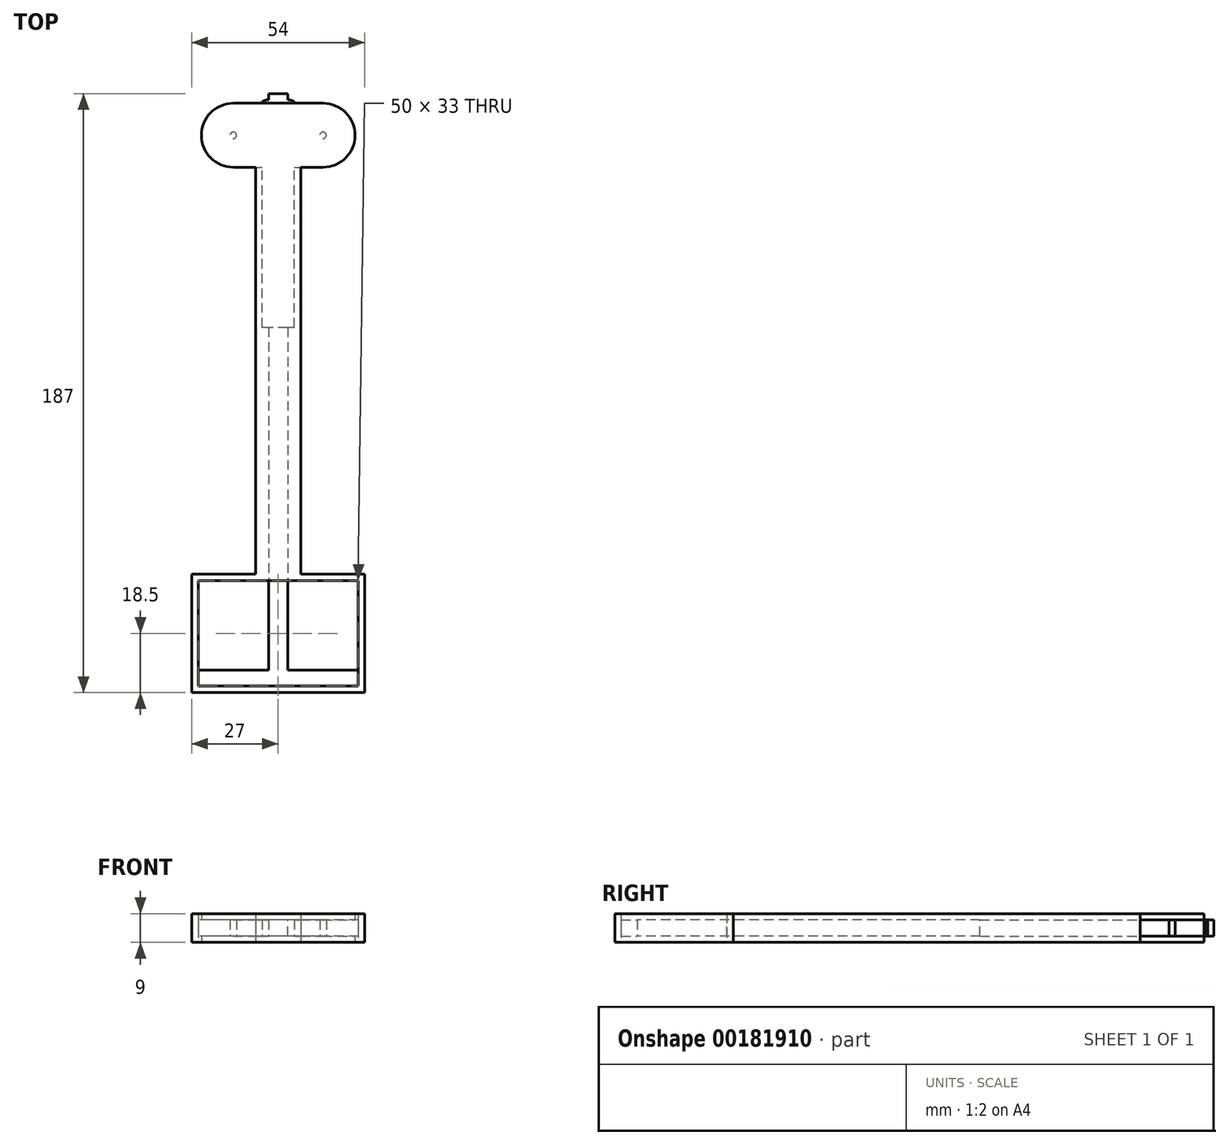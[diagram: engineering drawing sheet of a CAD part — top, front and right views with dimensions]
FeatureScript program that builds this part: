
annotation { "Feature Type Name" : "Feature", "Feature Type Description" : "" }
export const myFeature = defineFeature(function(context is Context, id is Id, definition is map)
    precondition{}
    {
        {
            var Q0;
            Q0=qCreatedBy(makeId("Top.planeOp"),FACE);
            var sketch = newSketch(context, id + "F0", { "sketchPlane" : qUnion([Q0])});
            skLineSegment(sketch, "E0.bottom", {"start": v(3, 13) * mm, "end": v(0, 13) * mm});
            skLineSegment(sketch, "E0.top", {"start": v(3, -167) * mm, "end": v(0, -167) * mm});
            skLineSegment(sketch, "E0.left", {"start": v(3, 13) * mm, "end": v(3, -167) * mm});
            skLineSegment(sketch, "E0.right", {"start": v(0, 13) * mm, "end": v(0, -167) * mm});
            skLineSegment(sketch, "E1", {"start": v(0, 10) * mm, "end": v(3, 10) * mm, "construction": true});
            skArc(sketch, "E2", {"start": v(3, 11.09) * mm, "mid": v(4.04, 10.94) * mm, "end": v(5, 10.5) * mm});
            skLineSegment(sketch, "E3", {"start": v(5, 10.5) * mm, "end": v(5, 10) * mm});
            skArc(sketch, "E4.MirrorCS", {"start": v(3, 8.91) * mm, "mid": v(4.04, 9.06) * mm, "end": v(5, 9.5) * mm});
            skLineSegment(sketch, "E5.MirrorCS", {"start": v(5, 9.5) * mm, "end": v(5, 10) * mm});
            skArc(sketch, "E6.1.0.0", {"start": v(3, 7.89) * mm, "mid": v(4.04, 7.74) * mm, "end": v(5, 7.3) * mm});
            skLineSegment(sketch, "E6.1.0.1", {"start": v(5, 7.3) * mm, "end": v(5, 6.8) * mm});
            skLineSegment(sketch, "E6.1.0.2", {"start": v(5, 6.3) * mm, "end": v(5, 6.8) * mm});
            skArc(sketch, "E6.1.0.3", {"start": v(3, 5.71) * mm, "mid": v(4.04, 5.86) * mm, "end": v(5, 6.3) * mm});
            skArc(sketch, "E6.2.0.0", {"start": v(3, 4.69) * mm, "mid": v(4.04, 4.54) * mm, "end": v(5, 4.1) * mm});
            skLineSegment(sketch, "E6.2.0.1", {"start": v(5, 4.1) * mm, "end": v(5, 3.6) * mm});
            skLineSegment(sketch, "E6.2.0.2", {"start": v(5, 3.1) * mm, "end": v(5, 3.6) * mm});
            skArc(sketch, "E6.2.0.3", {"start": v(3, 2.51) * mm, "mid": v(4.04, 2.66) * mm, "end": v(5, 3.1) * mm});
            skLineSegment(sketch, "E6.direction1", {"start": v(3, 7.39) * mm, "end": v(3, 4.19) * mm, "construction": true});
            skArc(sketch, "E7.0.3.0", {"start": v(3, 1.49) * mm, "mid": v(4.04, 1.34) * mm, "end": v(5, 0.9) * mm});
            skLineSegment(sketch, "E7.4.3.0", {"start": v(5, 0.9) * mm, "end": v(5, 0.4) * mm});
            skLineSegment(sketch, "E7.7.3.0", {"start": v(5, -0.1) * mm, "end": v(5, 0.4) * mm});
            skArc(sketch, "E7.10.3.0", {"start": v(3, -0.69) * mm, "mid": v(4.04, -0.54) * mm, "end": v(5, -0.1) * mm});
            skArc(sketch, "E7.0.4.0", {"start": v(3, -1.71) * mm, "mid": v(4.04, -1.86) * mm, "end": v(5, -2.3) * mm});
            skLineSegment(sketch, "E7.4.4.0", {"start": v(5, -2.3) * mm, "end": v(5, -2.8) * mm});
            skLineSegment(sketch, "E7.7.4.0", {"start": v(5, -3.3) * mm, "end": v(5, -2.8) * mm});
            skArc(sketch, "E7.10.4.0", {"start": v(3, -3.89) * mm, "mid": v(4.04, -3.74) * mm, "end": v(5, -3.3) * mm});
            skArc(sketch, "E7.0.5.0", {"start": v(3, -4.91) * mm, "mid": v(4.04, -5.06) * mm, "end": v(5, -5.5) * mm});
            skLineSegment(sketch, "E7.4.5.0", {"start": v(5, -5.5) * mm, "end": v(5, -6) * mm});
            skLineSegment(sketch, "E7.7.5.0", {"start": v(5, -6.5) * mm, "end": v(5, -6) * mm});
            skArc(sketch, "E7.10.5.0", {"start": v(3, -7.09) * mm, "mid": v(4.04, -6.94) * mm, "end": v(5, -6.5) * mm});
            skArc(sketch, "E7.0.6.0", {"start": v(3, -8.11) * mm, "mid": v(4.04, -8.26) * mm, "end": v(5, -8.7) * mm});
            skLineSegment(sketch, "E7.4.6.0", {"start": v(5, -8.7) * mm, "end": v(5, -9.2) * mm});
            skLineSegment(sketch, "E7.7.6.0", {"start": v(5, -9.7) * mm, "end": v(5, -9.2) * mm});
            skArc(sketch, "E7.10.6.0", {"start": v(3, -10.29) * mm, "mid": v(4.04, -10.14) * mm, "end": v(5, -9.7) * mm});
            skArc(sketch, "E7.0.7.0", {"start": v(3, -11.31) * mm, "mid": v(4.04, -11.46) * mm, "end": v(5, -11.9) * mm});
            skLineSegment(sketch, "E7.4.7.0", {"start": v(5, -11.9) * mm, "end": v(5, -12.4) * mm});
            skLineSegment(sketch, "E7.7.7.0", {"start": v(5, -12.9) * mm, "end": v(5, -12.4) * mm});
            skArc(sketch, "E7.10.7.0", {"start": v(3, -13.49) * mm, "mid": v(4.04, -13.34) * mm, "end": v(5, -12.9) * mm});
            skArc(sketch, "E7.0.8.0", {"start": v(3, -14.51) * mm, "mid": v(4.04, -14.66) * mm, "end": v(5, -15.1) * mm});
            skLineSegment(sketch, "E7.4.8.0", {"start": v(5, -15.1) * mm, "end": v(5, -15.6) * mm});
            skLineSegment(sketch, "E7.7.8.0", {"start": v(5, -16.1) * mm, "end": v(5, -15.6) * mm});
            skArc(sketch, "E7.10.8.0", {"start": v(3, -16.69) * mm, "mid": v(4.04, -16.54) * mm, "end": v(5, -16.1) * mm});
            skArc(sketch, "E7.0.9.0", {"start": v(3, -17.71) * mm, "mid": v(4.04, -17.86) * mm, "end": v(5, -18.3) * mm});
            skLineSegment(sketch, "E7.4.9.0", {"start": v(5, -18.3) * mm, "end": v(5, -18.8) * mm});
            skLineSegment(sketch, "E7.7.9.0", {"start": v(5, -19.3) * mm, "end": v(5, -18.8) * mm});
            skArc(sketch, "E7.10.9.0", {"start": v(3, -19.89) * mm, "mid": v(4.04, -19.74) * mm, "end": v(5, -19.3) * mm});
            skArc(sketch, "E7.0.10.0", {"start": v(3, -20.91) * mm, "mid": v(4.04, -21.06) * mm, "end": v(5, -21.5) * mm});
            skLineSegment(sketch, "E7.4.10.0", {"start": v(5, -21.5) * mm, "end": v(5, -22) * mm});
            skLineSegment(sketch, "E7.7.10.0", {"start": v(5, -22.5) * mm, "end": v(5, -22) * mm});
            skArc(sketch, "E7.10.10.0", {"start": v(3, -23.09) * mm, "mid": v(4.04, -22.94) * mm, "end": v(5, -22.5) * mm});
            skArc(sketch, "E7.0.11.0", {"start": v(3, -24.11) * mm, "mid": v(4.04, -24.26) * mm, "end": v(5, -24.7) * mm});
            skLineSegment(sketch, "E7.4.11.0", {"start": v(5, -24.7) * mm, "end": v(5, -25.2) * mm});
            skLineSegment(sketch, "E7.7.11.0", {"start": v(5, -25.7) * mm, "end": v(5, -25.2) * mm});
            skArc(sketch, "E7.10.11.0", {"start": v(3, -26.29) * mm, "mid": v(4.04, -26.14) * mm, "end": v(5, -25.7) * mm});
            skArc(sketch, "E7.0.12.0", {"start": v(3, -27.31) * mm, "mid": v(4.04, -27.46) * mm, "end": v(5, -27.9) * mm});
            skLineSegment(sketch, "E7.4.12.0", {"start": v(5, -27.9) * mm, "end": v(5, -28.4) * mm});
            skLineSegment(sketch, "E7.7.12.0", {"start": v(5, -28.9) * mm, "end": v(5, -28.4) * mm});
            skArc(sketch, "E7.10.12.0", {"start": v(3, -29.49) * mm, "mid": v(4.04, -29.34) * mm, "end": v(5, -28.9) * mm});
            skArc(sketch, "E7.0.13.0", {"start": v(3, -30.51) * mm, "mid": v(4.04, -30.66) * mm, "end": v(5, -31.1) * mm});
            skLineSegment(sketch, "E7.4.13.0", {"start": v(5, -31.1) * mm, "end": v(5, -31.6) * mm});
            skLineSegment(sketch, "E7.7.13.0", {"start": v(5, -32.1) * mm, "end": v(5, -31.6) * mm});
            skArc(sketch, "E7.10.13.0", {"start": v(3, -32.69) * mm, "mid": v(4.04, -32.54) * mm, "end": v(5, -32.1) * mm});
            skArc(sketch, "E7.0.14.0", {"start": v(3, -33.71) * mm, "mid": v(4.04, -33.86) * mm, "end": v(5, -34.3) * mm});
            skLineSegment(sketch, "E7.4.14.0", {"start": v(5, -34.3) * mm, "end": v(5, -34.8) * mm});
            skLineSegment(sketch, "E7.7.14.0", {"start": v(5, -35.3) * mm, "end": v(5, -34.8) * mm});
            skArc(sketch, "E7.10.14.0", {"start": v(3, -35.89) * mm, "mid": v(4.04, -35.74) * mm, "end": v(5, -35.3) * mm});
            skArc(sketch, "E7.0.15.0", {"start": v(3, -36.91) * mm, "mid": v(4.04, -37.06) * mm, "end": v(5, -37.5) * mm});
            skLineSegment(sketch, "E7.4.15.0", {"start": v(5, -37.5) * mm, "end": v(5, -38) * mm});
            skLineSegment(sketch, "E7.7.15.0", {"start": v(5, -38.5) * mm, "end": v(5, -38) * mm});
            skArc(sketch, "E7.10.15.0", {"start": v(3, -39.09) * mm, "mid": v(4.04, -38.94) * mm, "end": v(5, -38.5) * mm});
            skSolve(sketch);
        }
        {
            var Q0;
            Q0 = qSketchRegion(id + "F0", true);
            extrude(context, id + "F1", {"entities" : qUnion([Q0]), "depth" : 5 * mm});
        }
        {
            var Q0;
            Q0=makeQuery(id+"F1.opExtrude","SWEPT_BODY",BODY,{"disambiguationData":[OSD([sQuery(id+"F0.wireOp",EDGE,"E0.bottom"),sQuery(id+"F0.wireOp",EDGE,"E0.top"),sQuery(id+"F0.wireOp",EDGE,"E0.left"),sQuery(id+"F0.wireOp",EDGE,"E0.right"),sQuery(id+"F0.wireOp",EDGE,"E2"),sQuery(id+"F0.wireOp",EDGE,"E3"),sQuery(id+"F0.wireOp",EDGE,"E4.MirrorCS"),sQuery(id+"F0.wireOp",EDGE,"E5.MirrorCS"),sQuery(id+"F0.wireOp",EDGE,"E6.1.0.0"),sQuery(id+"F0.wireOp",EDGE,"E6.1.0.1"),sQuery(id+"F0.wireOp",EDGE,"E6.1.0.2"),sQuery(id+"F0.wireOp",EDGE,"E6.1.0.3"),sQuery(id+"F0.wireOp",EDGE,"E6.2.0.0"),sQuery(id+"F0.wireOp",EDGE,"E6.2.0.1"),sQuery(id+"F0.wireOp",EDGE,"E6.2.0.2"),sQuery(id+"F0.wireOp",EDGE,"E6.2.0.3"),sQuery(id+"F0.wireOp",EDGE,"E7.0.3.0"),sQuery(id+"F0.wireOp",EDGE,"E7.4.3.0"),sQuery(id+"F0.wireOp",EDGE,"E7.7.3.0"),sQuery(id+"F0.wireOp",EDGE,"E7.10.3.0"),sQuery(id+"F0.wireOp",EDGE,"E7.0.4.0"),sQuery(id+"F0.wireOp",EDGE,"E7.4.4.0"),sQuery(id+"F0.wireOp",EDGE,"E7.7.4.0"),sQuery(id+"F0.wireOp",EDGE,"E7.10.4.0"),sQuery(id+"F0.wireOp",EDGE,"E7.0.5.0"),sQuery(id+"F0.wireOp",EDGE,"E7.4.5.0"),sQuery(id+"F0.wireOp",EDGE,"E7.7.5.0"),sQuery(id+"F0.wireOp",EDGE,"E7.10.5.0"),sQuery(id+"F0.wireOp",EDGE,"E7.0.6.0"),sQuery(id+"F0.wireOp",EDGE,"E7.4.6.0"),sQuery(id+"F0.wireOp",EDGE,"E7.7.6.0"),sQuery(id+"F0.wireOp",EDGE,"E7.10.6.0"),sQuery(id+"F0.wireOp",EDGE,"E7.0.7.0"),sQuery(id+"F0.wireOp",EDGE,"E7.4.7.0"),sQuery(id+"F0.wireOp",EDGE,"E7.7.7.0"),sQuery(id+"F0.wireOp",EDGE,"E7.10.7.0"),sQuery(id+"F0.wireOp",EDGE,"E7.0.8.0"),sQuery(id+"F0.wireOp",EDGE,"E7.4.8.0"),sQuery(id+"F0.wireOp",EDGE,"E7.7.8.0"),sQuery(id+"F0.wireOp",EDGE,"E7.10.8.0"),sQuery(id+"F0.wireOp",EDGE,"E7.0.9.0"),sQuery(id+"F0.wireOp",EDGE,"E7.4.9.0"),sQuery(id+"F0.wireOp",EDGE,"E7.7.9.0"),sQuery(id+"F0.wireOp",EDGE,"E7.10.9.0"),sQuery(id+"F0.wireOp",EDGE,"E7.0.10.0"),sQuery(id+"F0.wireOp",EDGE,"E7.4.10.0"),sQuery(id+"F0.wireOp",EDGE,"E7.7.10.0"),sQuery(id+"F0.wireOp",EDGE,"E7.10.10.0"),sQuery(id+"F0.wireOp",EDGE,"E7.0.11.0"),sQuery(id+"F0.wireOp",EDGE,"E7.4.11.0"),sQuery(id+"F0.wireOp",EDGE,"E7.7.11.0"),sQuery(id+"F0.wireOp",EDGE,"E7.10.11.0"),sQuery(id+"F0.wireOp",EDGE,"E7.0.12.0"),sQuery(id+"F0.wireOp",EDGE,"E7.4.12.0"),sQuery(id+"F0.wireOp",EDGE,"E7.7.12.0"),sQuery(id+"F0.wireOp",EDGE,"E7.10.12.0"),sQuery(id+"F0.wireOp",EDGE,"E7.0.13.0"),sQuery(id+"F0.wireOp",EDGE,"E7.4.13.0"),sQuery(id+"F0.wireOp",EDGE,"E7.7.13.0"),sQuery(id+"F0.wireOp",EDGE,"E7.10.13.0"),sQuery(id+"F0.wireOp",EDGE,"E7.0.14.0"),sQuery(id+"F0.wireOp",EDGE,"E7.4.14.0"),sQuery(id+"F0.wireOp",EDGE,"E7.7.14.0"),sQuery(id+"F0.wireOp",EDGE,"E7.10.14.0"),sQuery(id+"F0.wireOp",EDGE,"E7.0.15.0"),sQuery(id+"F0.wireOp",EDGE,"E7.4.15.0"),sQuery(id+"F0.wireOp",EDGE,"E7.7.15.0"),sQuery(id+"F0.wireOp",EDGE,"E7.10.15.0")])]});
            var Q1;
            Q1=makeQuery(id+"F1.opExtrude","SWEPT_FACE",FACE,{"disambiguationData":[OSD([sQuery(id+"F0.wireOp",EDGE,"E0.right")])]});
            mirror(context, id + "F2", {"operationType" : NewBodyOperationType.ADD, "entities" : qUnion([Q0]), "mirrorPlane" : qUnion([Q1])});
        }
        {
            var Q0;
            {var subQ0=makeQuery(id+"F1.opExtrude","SWEPT_FACE",FACE,{"disambiguationData":[OSD([sQuery(id+"F0.wireOp",EDGE,"E0.top")])]});Q0=makeQuery(id+"F2.boolean.opBoolean","MERGE",FACE,{"derivedFrom":[subQ0,makeQuery(id+"F2.opPattern","COPY",FACE,{"derivedFrom":subQ0,"instanceName":"1"})]});}
            var sketch = newSketch(context, id + "F3", { "sketchPlane" : qUnion([Q0])});
            skLineSegment(sketch, "E8.bottom", {"start": v(25, 5) * mm, "end": v(-25, 5) * mm});
            skLineSegment(sketch, "E8.top", {"start": v(25, 0) * mm, "end": v(-25, 0) * mm});
            skLineSegment(sketch, "E8.left", {"start": v(25, 5) * mm, "end": v(25, 0) * mm});
            skLineSegment(sketch, "E8.right", {"start": v(-25, 5) * mm, "end": v(-25, 0) * mm});
            skPoint(sketch, "E8.middle", {"position": v(0, 2.5) * mm});
            skPoint(sketch, "E8.middle.positionSnap0", {"position": v(-3, 2.5) * mm});
            skPoint(sketch, "E8.middle.positionSnap1", {"position": v(0, 5) * mm});
            skPoint(sketch, "E8.centerSnap0", {"position": v(-3, 2.5) * mm});
            skPoint(sketch, "E8.centerSnap1", {"position": v(0, 5) * mm});
            skSolve(sketch);
        }
        {
            var Q0;
            Q0 = qSketchRegion(id + "F3", true);
            extrude(context, id + "F4", {"entities" : qUnion([Q0]), "operationType" : NewBodyOperationType.ADD, "depth" : 5 * mm});
        }
        {
            var Q0;
            Q0=qCreatedBy(makeId("Top.planeOp"),FACE);
            var sketch = newSketch(context, id + "F5", { "sketchPlane" : qUnion([Q0])});
            skCircle(sketch, "E9", {"center": v(14, 0) * mm, "radius": 10 * mm});
            skLineSegment(sketch, "E10", {"start": v(14, 10) * mm, "end": v(0, 10) * mm});
            skLineSegment(sketch, "E11", {"start": v(14, -10) * mm, "end": v(7, -10) * mm});
            skLineSegment(sketch, "E12", {"start": v(7, -10) * mm, "end": v(7, -137) * mm});
            skLineSegment(sketch, "E13", {"start": v(7, -137) * mm, "end": v(27, -137) * mm});
            skLineSegment(sketch, "E14", {"start": v(27, -137) * mm, "end": v(27, -174) * mm});
            skLineSegment(sketch, "E15", {"start": v(27, -174) * mm, "end": v(0, -174) * mm});
            skLineSegment(sketch, "E16.MirrorCS", {"start": v(-14, 10) * mm, "end": v(0, 10) * mm});
            skCircle(sketch, "E17.MirrorC", {"center": v(-14, 0) * mm, "radius": 10 * mm});
            skLineSegment(sketch, "E18.MirrorCS", {"start": v(-14, -10) * mm, "end": v(-7, -10) * mm});
            skLineSegment(sketch, "E19.MirrorCS", {"start": v(-7, -10) * mm, "end": v(-7, -137) * mm});
            skLineSegment(sketch, "E20.MirrorCS", {"start": v(-7, -137) * mm, "end": v(-27, -137) * mm});
            skLineSegment(sketch, "E21.MirrorCS", {"start": v(-27, -137) * mm, "end": v(-27, -174) * mm});
            skLineSegment(sketch, "E22.MirrorCS", {"start": v(-27, -174) * mm, "end": v(0, -174) * mm});
            skLineSegment(sketch, "E23.bottom", {"start": v(25, -172) * mm, "end": v(-25, -172) * mm});
            skLineSegment(sketch, "E23.top", {"start": v(25, -139) * mm, "end": v(-25, -139) * mm});
            skLineSegment(sketch, "E23.left", {"start": v(25, -172) * mm, "end": v(25, -139) * mm});
            skLineSegment(sketch, "E23.right", {"start": v(-25, -172) * mm, "end": v(-25, -139) * mm});
            skPoint(sketch, "E23.middle", {"position": v(0, -155.5) * mm});
            skSolve(sketch);
        }
        {
            var Q0;
            Q0 = qSketchRegion(id + "F5", true);
            extrude(context, id + "F6", {"entities" : qUnion([Q0]), "depth" : 7 * mm, "hasSecondDirection" : true, "secondDirectionOppositeDirection" : true, "secondDirectionDepth" : 2 * mm});
        }
        {
            var Q0;
            Q0=makeQuery(id+"F1.opExtrude","SWEPT_BODY",BODY,{"disambiguationData":[OSD([sQuery(id+"F0.wireOp",EDGE,"E0.bottom"),sQuery(id+"F0.wireOp",EDGE,"E0.top"),sQuery(id+"F0.wireOp",EDGE,"E0.left"),sQuery(id+"F0.wireOp",EDGE,"E0.right"),sQuery(id+"F0.wireOp",EDGE,"E2"),sQuery(id+"F0.wireOp",EDGE,"E3"),sQuery(id+"F0.wireOp",EDGE,"E4.MirrorCS"),sQuery(id+"F0.wireOp",EDGE,"E5.MirrorCS"),sQuery(id+"F0.wireOp",EDGE,"E6.1.0.0"),sQuery(id+"F0.wireOp",EDGE,"E6.1.0.1"),sQuery(id+"F0.wireOp",EDGE,"E6.1.0.2"),sQuery(id+"F0.wireOp",EDGE,"E6.1.0.3"),sQuery(id+"F0.wireOp",EDGE,"E6.2.0.0"),sQuery(id+"F0.wireOp",EDGE,"E6.2.0.1"),sQuery(id+"F0.wireOp",EDGE,"E6.2.0.2"),sQuery(id+"F0.wireOp",EDGE,"E6.2.0.3"),sQuery(id+"F0.wireOp",EDGE,"E7.0.3.0"),sQuery(id+"F0.wireOp",EDGE,"E7.4.3.0"),sQuery(id+"F0.wireOp",EDGE,"E7.7.3.0"),sQuery(id+"F0.wireOp",EDGE,"E7.10.3.0"),sQuery(id+"F0.wireOp",EDGE,"E7.0.4.0"),sQuery(id+"F0.wireOp",EDGE,"E7.4.4.0"),sQuery(id+"F0.wireOp",EDGE,"E7.7.4.0"),sQuery(id+"F0.wireOp",EDGE,"E7.10.4.0"),sQuery(id+"F0.wireOp",EDGE,"E7.0.5.0"),sQuery(id+"F0.wireOp",EDGE,"E7.4.5.0"),sQuery(id+"F0.wireOp",EDGE,"E7.7.5.0"),sQuery(id+"F0.wireOp",EDGE,"E7.10.5.0"),sQuery(id+"F0.wireOp",EDGE,"E7.0.6.0"),sQuery(id+"F0.wireOp",EDGE,"E7.4.6.0"),sQuery(id+"F0.wireOp",EDGE,"E7.7.6.0"),sQuery(id+"F0.wireOp",EDGE,"E7.10.6.0"),sQuery(id+"F0.wireOp",EDGE,"E7.0.7.0"),sQuery(id+"F0.wireOp",EDGE,"E7.4.7.0"),sQuery(id+"F0.wireOp",EDGE,"E7.7.7.0"),sQuery(id+"F0.wireOp",EDGE,"E7.10.7.0"),sQuery(id+"F0.wireOp",EDGE,"E7.0.8.0"),sQuery(id+"F0.wireOp",EDGE,"E7.4.8.0"),sQuery(id+"F0.wireOp",EDGE,"E7.7.8.0"),sQuery(id+"F0.wireOp",EDGE,"E7.10.8.0"),sQuery(id+"F0.wireOp",EDGE,"E7.0.9.0"),sQuery(id+"F0.wireOp",EDGE,"E7.4.9.0"),sQuery(id+"F0.wireOp",EDGE,"E7.7.9.0"),sQuery(id+"F0.wireOp",EDGE,"E7.10.9.0"),sQuery(id+"F0.wireOp",EDGE,"E7.0.10.0"),sQuery(id+"F0.wireOp",EDGE,"E7.4.10.0"),sQuery(id+"F0.wireOp",EDGE,"E7.7.10.0"),sQuery(id+"F0.wireOp",EDGE,"E7.10.10.0"),sQuery(id+"F0.wireOp",EDGE,"E7.0.11.0"),sQuery(id+"F0.wireOp",EDGE,"E7.4.11.0"),sQuery(id+"F0.wireOp",EDGE,"E7.7.11.0"),sQuery(id+"F0.wireOp",EDGE,"E7.10.11.0"),sQuery(id+"F0.wireOp",EDGE,"E7.0.12.0"),sQuery(id+"F0.wireOp",EDGE,"E7.4.12.0"),sQuery(id+"F0.wireOp",EDGE,"E7.7.12.0"),sQuery(id+"F0.wireOp",EDGE,"E7.10.12.0"),sQuery(id+"F0.wireOp",EDGE,"E7.0.13.0"),sQuery(id+"F0.wireOp",EDGE,"E7.4.13.0"),sQuery(id+"F0.wireOp",EDGE,"E7.7.13.0"),sQuery(id+"F0.wireOp",EDGE,"E7.10.13.0"),sQuery(id+"F0.wireOp",EDGE,"E7.0.14.0"),sQuery(id+"F0.wireOp",EDGE,"E7.4.14.0"),sQuery(id+"F0.wireOp",EDGE,"E7.7.14.0"),sQuery(id+"F0.wireOp",EDGE,"E7.10.14.0"),sQuery(id+"F0.wireOp",EDGE,"E7.0.15.0"),sQuery(id+"F0.wireOp",EDGE,"E7.4.15.0"),sQuery(id+"F0.wireOp",EDGE,"E7.7.15.0"),sQuery(id+"F0.wireOp",EDGE,"E7.10.15.0")])]});
            var Q1;
            Q1=makeQuery(id+"F6.opExtrude","SWEPT_BODY",BODY,{"disambiguationData":[OSD([sQuery(id+"F5.wireOp",EDGE,"E9"),sQuery(id+"F5.wireOp",EDGE,"E10"),sQuery(id+"F5.wireOp",EDGE,"E11"),sQuery(id+"F5.wireOp",EDGE,"E12"),sQuery(id+"F5.wireOp",EDGE,"E13"),sQuery(id+"F5.wireOp",EDGE,"E14"),sQuery(id+"F5.wireOp",EDGE,"E15"),sQuery(id+"F5.wireOp",EDGE,"E16.MirrorCS"),sQuery(id+"F5.wireOp",EDGE,"E17.MirrorC"),sQuery(id+"F5.wireOp",EDGE,"E18.MirrorCS"),sQuery(id+"F5.wireOp",EDGE,"E19.MirrorCS"),sQuery(id+"F5.wireOp",EDGE,"E20.MirrorCS"),sQuery(id+"F5.wireOp",EDGE,"E21.MirrorCS"),sQuery(id+"F5.wireOp",EDGE,"E22.MirrorCS"),sQuery(id+"F5.wireOp",EDGE,"E23.bottom"),sQuery(id+"F5.wireOp",EDGE,"E23.top"),sQuery(id+"F5.wireOp",EDGE,"E23.left"),sQuery(id+"F5.wireOp",EDGE,"E23.right")])]});
            booleanBodies(context, id + "F7", {"operationType" : BooleanOperationType.SUBTRACTION, "tools" : qUnion([Q0]), "targets" : qUnion([Q1]), "keepTools" : true});
        }
        {
            var Q0;
            Q0=qCreatedBy(makeId("Top.planeOp"),FACE);
            var sketch = newSketch(context, id + "F8", { "sketchPlane" : qUnion([Q0])});
            skArc(sketch, "E24.0", {"start": v(-14, -10) * mm, "mid": v(-24, 0) * mm, "end": v(-14, 10) * mm});
            skLineSegment(sketch, "E25.0", {"start": v(14, 10) * mm, "end": v(-14, 10) * mm});
            skArc(sketch, "E26.0", {"start": v(14, -10) * mm, "mid": v(24, 0) * mm, "end": v(14, 10) * mm});
            skLineSegment(sketch, "E27", {"start": v(-14, -10) * mm, "end": v(14, -10) * mm});
            skSolve(sketch);
        }
        {
            var Q0;
            Q0 = qSketchRegion(id + "F8", true);
            extrude(context, id + "F9", {"entities" : qUnion([Q0]), "operationType" : NewBodyOperationType.REMOVE, "depth" : 5 * mm});
        }
        {
            var Q0;
            {var subQ69=sQuery(id+"F8.wireOp",EDGE,"E27");Q0=makeQuery(id+"F9.boolean.opBoolean","COPY",FACE,{"disambiguationData":[TD([makeQuery(id+"F6.opExtrude","SWEPT_FACE",FACE,{"disambiguationData":[OSD([sQuery(id+"F5.wireOp",EDGE,"E18.MirrorCS")])]})])],"derivedFrom":makeQuery(id+"F9.opExtrude","SWEPT_FACE",FACE,{"disambiguationData":[OSD([subQ69])]})});}
            var sketch = newSketch(context, id + "F10", { "sketchPlane" : qUnion([Q0])});
            skLineSegment(sketch, "E28.bottom", {"start": v(-5, 5) * mm, "end": v(5, 5) * mm});
            skLineSegment(sketch, "E28.top", {"start": v(-5, 0) * mm, "end": v(5, 0) * mm});
            skLineSegment(sketch, "E28.left", {"start": v(-5, 5) * mm, "end": v(-5, 0) * mm});
            skLineSegment(sketch, "E28.right", {"start": v(5, 5) * mm, "end": v(5, 0) * mm});
            skSolve(sketch);
        }
        {
            var Q0;
            Q0 = qSketchRegion(id + "F10", true);
            extrude(context, id + "F11", {"entities" : qUnion([Q0]), "operationType" : NewBodyOperationType.REMOVE, "oppositeDirection" : true, "depth" : 50 * mm});
        }
        {
            var Q0;
            Q0=qCreatedBy(makeId("Top.planeOp"),FACE);
            var sketch = newSketch(context, id + "F12", { "sketchPlane" : qUnion([Q0])});
            skCircle(sketch, "E29", {"center": v(-14, 0) * mm, "radius": 1 * mm});
            skCircle(sketch, "E30", {"center": v(14, 0) * mm, "radius": 1 * mm});
            skSolve(sketch);
        }
        {
            var Q0;
            Q0 = qSketchRegion(id + "F12", true);
            extrude(context, id + "F13", {"entities" : qUnion([Q0]), "operationType" : NewBodyOperationType.ADD, "endBound" : BoundingType.UP_TO_NEXT, "depth" : 25 * mm});
        }
    });
